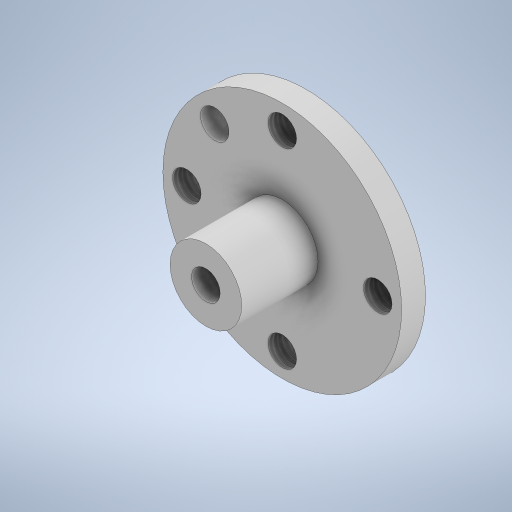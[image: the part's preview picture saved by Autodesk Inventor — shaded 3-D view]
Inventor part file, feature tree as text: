
AUTODESK INVENTOR PART (.ipt)
format: ipt  version: 2023 (Build 270158000, 158)  size: 285,184 bytes
history: native  units: mm
features: sketch x5, thread x4, extrude x3, hole x1, pattern_circular x1, projected_geometry x1
ambient origin geometry x8: Origin, YZ Plane, XZ Plane, XY Plane, X Axis, Y Axis, Z Axis, Center Point
bodies: Solid1 (feature_tree)
feature tree (15):
  extrude  "Extrusion1"  Depth=5.0mm TaperAngle=0.0deg
  hole  "Hole1"  [1 undecoded]
  thread  "Thread1"  [1 undecoded]
  thread  "Thread2"  [1 undecoded]
  thread  "Thread3"  [1 undecoded]
  thread  "Thread4"  [1 undecoded]
  sketch  "Sketch3"  dims[d8=6.0mm d9=6.0mm d10=4.0mm d11=2.0mm d12=90.0deg d13=8.0mm d14=20.594885mm d15=10.0mm d16=0.0mm d17=10.0mm d18=0.0mm]
  pattern_circular  "Circular Pattern1"  Count=2 Angle=45.0deg
  extrude  "Extrusion2"  Depth=5.0mm TaperAngle=0.0deg
  extrude  "Extrusion3"  Depth=16.0mm
  sketch  "Sketch1"  dims[d0=50.0mm d1=5.0mm d2=0.0mm]
  sketch  "Sketch2"  dims[d4=6.0mm d5=6.0mm d6=6.0mm d7=6.0mm]
  sketch  "Sketch4"  dims[d19=10.0mm d20=0.0mm]
  sketch  "Sketch5"  dims[d21=10.0mm d22=0.0mm d24=20.0mm d25=45.0deg d27=5.0mm d28=0.0mm d29=15.0mm d30=6.0mm d31=16.0mm d32=0.0mm]
  projected_geometry  "Projected Loop1"
note: 5 required parameter values undecoded (feature->parameter linkage not recoverable at this tier; creation-order binding heuristic only, values carry confidence <= 0.55)
